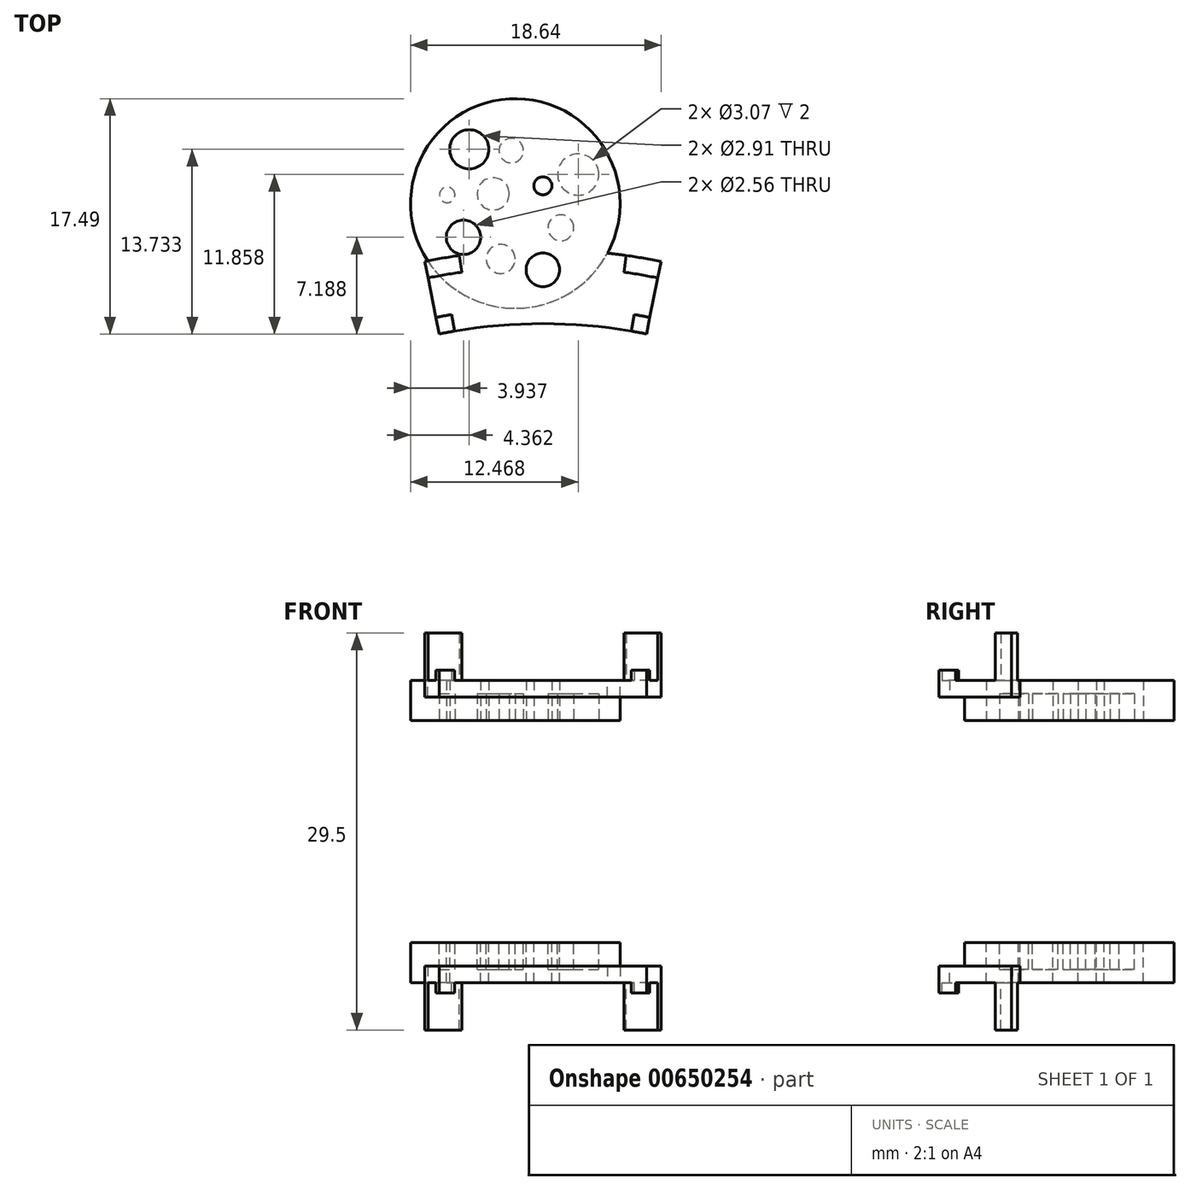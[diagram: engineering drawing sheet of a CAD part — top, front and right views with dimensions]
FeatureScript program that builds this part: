
annotation { "Feature Type Name" : "Feature", "Feature Type Description" : "" }
export const myFeature = defineFeature(function(context is Context, id is Id, definition is map)
    precondition{}
    {
        {
            var Q0;
            Q0=qCreatedBy(makeId("Top.planeOp"),FACE);
            var sketch = newSketch(context, id + "F0", { "sketchPlane" : qUnion([Q0])});
            skCircle(sketch, "E0", {"center": v(0, 0) * mm, "radius": 39 * mm});
            skCircle(sketch, "E1", {"center": v(0, 0) * mm, "radius": 44.5 * mm});
            skCircle(sketch, "E2", {"center": v(0, 43) * mm, "radius": 1.25 * mm});
            skCircle(sketch, "E3", {"center": v(0, 43) * mm, "radius": 6 * mm});
            skLineSegment(sketch, "E4", {"start": v(-7.7, 38.23) * mm, "end": v(-8.8, 43.62) * mm});
            skLineSegment(sketch, "E5", {"start": v(7.7, 38.23) * mm, "end": v(8.8, 43.62) * mm});
            skLineSegment(sketch, "E6", {"start": v(-7.5, 43.86) * mm, "end": v(-6.58, 38.44) * mm});
            skLineSegment(sketch, "E7", {"start": v(6.58, 38.44) * mm, "end": v(7.5, 43.86) * mm});
            skCircle(sketch, "E8", {"center": v(0, 0) * mm, "radius": 40.25 * mm});
            skCircle(sketch, "E9", {"center": v(0, 0) * mm, "radius": 43.25 * mm});
            skSolve(sketch);
        }
        {
            var Q0;
            {var subQ0=sQuery(id+"F0.wireOp",EDGE,"E7");var subQ1=sQuery(id+"F0.wireOp",EDGE,"E1");var subQ2=makeQuery(id+"F0.imprint","INTERSECT",VERTEX,{"derivedFrom":[subQ1,subQ0]});Q0=makeQuery(id+"F0.imprint","IMPRINT",FACE,{"disambiguationData":[TD([[makeQuery(id+"F0.imprint","IMPRINT",EDGE,{"disambiguationData":[TD([[subQ2,-1.0]])],"derivedFrom":subQ1}),1.0]])]});}
            var Q1;
            {var subQ0=sQuery(id+"F0.wireOp",EDGE,"E6");var subQ1=sQuery(id+"F0.wireOp",EDGE,"E1");var subQ2=makeQuery(id+"F0.imprint","INTERSECT",VERTEX,{"derivedFrom":[subQ1,subQ0]});Q1=makeQuery(id+"F0.imprint","IMPRINT",FACE,{"disambiguationData":[TD([[makeQuery(id+"F0.imprint","IMPRINT",EDGE,{"disambiguationData":[TD([[subQ2,1.0]])],"derivedFrom":subQ1}),1.0]])]});}
            var Q2;
            {var subQ0=sQuery(id+"F0.wireOp",EDGE,"E3");var subQ1=sQuery(id+"F0.wireOp",EDGE,"E1");var subQ2=makeQuery(id+"F0.imprint","INTERSECT",VERTEX,{"disambiguationData":[OD(0.0)],"derivedFrom":[subQ1,subQ0]});Q2=makeQuery(id+"F0.imprint","IMPRINT",FACE,{"disambiguationData":[TD([[makeQuery(id+"F0.imprint","IMPRINT",EDGE,{"disambiguationData":[TD([[subQ2,-1.0]])],"derivedFrom":subQ1}),1.0]])]});}
            var Q3;
            {var subQ0=sQuery(id+"F0.wireOp",EDGE,"E8");var subQ1=sQuery(id+"F0.wireOp",EDGE,"E3");var subQ2=makeQuery(id+"F0.imprint","INTERSECT",VERTEX,{"disambiguationData":[OD(1.0)],"derivedFrom":[subQ1,subQ0]});Q3=makeQuery(id+"F0.imprint","IMPRINT",FACE,{"disambiguationData":[TD([[makeQuery(id+"F0.imprint","IMPRINT",EDGE,{"disambiguationData":[TD([[subQ2,-1.0]])],"derivedFrom":subQ1}),-1.0]])]});}
            var Q4;
            {var subQ3=sQuery(id+"F0.wireOp",EDGE,"E9");var subQ5=sQuery(id+"F0.wireOp",EDGE,"E2");var subQ6=makeQuery(id+"F0.imprint","INTERSECT",VERTEX,{"disambiguationData":[OD(0.0)],"derivedFrom":[subQ5,subQ3]});Q4=makeQuery(id+"F0.imprint","IMPRINT",FACE,{"disambiguationData":[TD([[makeQuery(id+"F0.imprint","IMPRINT",EDGE,{"disambiguationData":[TD([[subQ6,1.0]])],"derivedFrom":subQ5}),-1.0]])]});}
            var Q5;
            {var subQ0=sQuery(id+"F0.wireOp",EDGE,"E9");var subQ1=sQuery(id+"F0.wireOp",EDGE,"E3");var subQ2=makeQuery(id+"F0.imprint","INTERSECT",VERTEX,{"disambiguationData":[OD(0.0)],"derivedFrom":[subQ1,subQ0]});Q5=makeQuery(id+"F0.imprint","IMPRINT",FACE,{"disambiguationData":[TD([[makeQuery(id+"F0.imprint","IMPRINT",EDGE,{"disambiguationData":[TD([[subQ2,-1.0]])],"derivedFrom":subQ1}),-1.0]])]});}
            var Q6;
            {var subQ0=sQuery(id+"F0.wireOp",EDGE,"E6");var subQ1=sQuery(id+"F0.wireOp",EDGE,"E0");var subQ2=makeQuery(id+"F0.imprint","INTERSECT",VERTEX,{"derivedFrom":[subQ1,subQ0]});Q6=makeQuery(id+"F0.imprint","IMPRINT",FACE,{"disambiguationData":[TD([[makeQuery(id+"F0.imprint","IMPRINT",EDGE,{"disambiguationData":[TD([[subQ2,1.0]])],"derivedFrom":subQ1}),-1.0]])]});}
            var Q7;
            {var subQ0=sQuery(id+"F0.wireOp",EDGE,"E3");var subQ1=sQuery(id+"F0.wireOp",EDGE,"E0");var subQ2=makeQuery(id+"F0.imprint","INTERSECT",VERTEX,{"disambiguationData":[OD(0.0)],"derivedFrom":[subQ1,subQ0]});Q7=makeQuery(id+"F0.imprint","IMPRINT",FACE,{"disambiguationData":[TD([[makeQuery(id+"F0.imprint","IMPRINT",EDGE,{"disambiguationData":[TD([[subQ2,-1.0]])],"derivedFrom":subQ1}),-1.0]])]});}
            var Q8;
            {var subQ0=sQuery(id+"F0.wireOp",EDGE,"E7");var subQ1=sQuery(id+"F0.wireOp",EDGE,"E0");var subQ2=makeQuery(id+"F0.imprint","INTERSECT",VERTEX,{"derivedFrom":[subQ1,subQ0]});Q8=makeQuery(id+"F0.imprint","IMPRINT",FACE,{"disambiguationData":[TD([[makeQuery(id+"F0.imprint","IMPRINT",EDGE,{"disambiguationData":[TD([[subQ2,-1.0]])],"derivedFrom":subQ1}),-1.0]])]});}
            var Q9;
            {var subQ0=sQuery(id+"F0.wireOp",EDGE,"E8");var subQ1=sQuery(id+"F0.wireOp",EDGE,"E5");var subQ2=makeQuery(id+"F0.imprint","INTERSECT",VERTEX,{"derivedFrom":[subQ1,subQ0]});Q9=makeQuery(id+"F0.imprint","IMPRINT",FACE,{"disambiguationData":[TD([[makeQuery(id+"F0.imprint","IMPRINT",EDGE,{"disambiguationData":[TD([[subQ2,-1.0]])],"derivedFrom":subQ1}),1.0]])]});}
            var Q10;
            {var subQ0=sQuery(id+"F0.wireOp",EDGE,"E8");var subQ1=sQuery(id+"F0.wireOp",EDGE,"E4");var subQ2=makeQuery(id+"F0.imprint","INTERSECT",VERTEX,{"derivedFrom":[subQ1,subQ0]});Q10=makeQuery(id+"F0.imprint","IMPRINT",FACE,{"disambiguationData":[TD([[makeQuery(id+"F0.imprint","IMPRINT",EDGE,{"disambiguationData":[TD([[subQ2,-1.0]])],"derivedFrom":subQ1}),-1.0]])]});}
            extrude(context, id + "F1", {"entities" : qUnion([Q0, Q1, Q2, Q3, Q4, Q5, Q6, Q7, Q8, Q9, Q10]), "depth" : 1.25 * mm, "offsetDistance" : 25 * mm});
        }
        {
            var Q0;
            Q0=qCreatedBy(makeId("Top.planeOp"),FACE);
            var sketch = newSketch(context, id + "F2", { "sketchPlane" : qUnion([Q0])});
            skCircle(sketch, "E10", {"center": v(0, 0) * mm, "radius": 39 * mm});
            skCircle(sketch, "E11", {"center": v(0, 0) * mm, "radius": 44.5 * mm});
            skCircle(sketch, "E12", {"center": v(0, 43) * mm, "radius": 0.85 * mm});
            skCircle(sketch, "E13", {"center": v(0, 43) * mm, "radius": 6 * mm});
            skLineSegment(sketch, "E14", {"start": v(-7.7, 38.23) * mm, "end": v(-8.8, 43.62) * mm});
            skLineSegment(sketch, "E15", {"start": v(7.7, 38.23) * mm, "end": v(8.8, 43.62) * mm});
            skLineSegment(sketch, "E16", {"start": v(-6.2, 44.06) * mm, "end": v(-5.44, 38.62) * mm});
            skLineSegment(sketch, "E17", {"start": v(5.44, 38.62) * mm, "end": v(6.2, 44.06) * mm});
            skCircle(sketch, "E18", {"center": v(0, 0) * mm, "radius": 40.25 * mm});
            skCircle(sketch, "E19", {"center": v(0, 0) * mm, "radius": 43.25 * mm});
            skSolve(sketch);
        }
        {
            var Q0;
            {var subQ0=sQuery(id+"F2.wireOp",EDGE,"E15");var subQ1=sQuery(id+"F2.wireOp",EDGE,"E11");var subQ2=makeQuery(id+"F2.imprint","INTERSECT",VERTEX,{"derivedFrom":[subQ1,subQ0]});Q0=makeQuery(id+"F2.imprint","IMPRINT",FACE,{"disambiguationData":[TD([[makeQuery(id+"F2.imprint","IMPRINT",EDGE,{"disambiguationData":[TD([[subQ2,-1.0]])],"derivedFrom":subQ1}),1.0]])]});}
            var Q1;
            {var subQ0=sQuery(id+"F2.wireOp",EDGE,"E14");var subQ1=sQuery(id+"F2.wireOp",EDGE,"E11");var subQ2=makeQuery(id+"F2.imprint","INTERSECT",VERTEX,{"derivedFrom":[subQ1,subQ0]});Q1=makeQuery(id+"F2.imprint","IMPRINT",FACE,{"disambiguationData":[TD([[makeQuery(id+"F2.imprint","IMPRINT",EDGE,{"disambiguationData":[TD([[subQ2,1.0]])],"derivedFrom":subQ1}),1.0]])]});}
            extrude(context, id + "F3", {"entities" : qUnion([Q0, Q1]), "operationType" : NewBodyOperationType.ADD, "depth" : 4.75 * mm, "offsetDistance" : 25 * mm});
        }
        {
            var Q0;
            Q0=qCreatedBy(makeId("Top.planeOp"),FACE);
            var sketch = newSketch(context, id + "F4", { "sketchPlane" : qUnion([Q0])});
            skCircle(sketch, "E20", {"center": v(0, 0) * mm, "radius": 39 * mm});
            skCircle(sketch, "E21", {"center": v(0, 0) * mm, "radius": 44.5 * mm});
            skCircle(sketch, "E22", {"center": v(0, 43) * mm, "radius": 0.85 * mm});
            skCircle(sketch, "E23", {"center": v(0, 43) * mm, "radius": 6 * mm});
            skLineSegment(sketch, "E24", {"start": v(-7.7, 38.23) * mm, "end": v(-8.8, 43.62) * mm});
            skLineSegment(sketch, "E25", {"start": v(7.7, 38.23) * mm, "end": v(8.8, 43.62) * mm});
            skLineSegment(sketch, "E26", {"start": v(-7.5, 43.86) * mm, "end": v(-6.58, 38.44) * mm});
            skLineSegment(sketch, "E27", {"start": v(6.58, 38.44) * mm, "end": v(7.5, 43.86) * mm});
            skCircle(sketch, "E28", {"center": v(0, 0) * mm, "radius": 40.25 * mm});
            skCircle(sketch, "E29", {"center": v(0, 0) * mm, "radius": 43.25 * mm});
            skSolve(sketch);
        }
        {
            var Q0;
            {var subQ0=sQuery(id+"F4.wireOp",EDGE,"E24");var subQ1=sQuery(id+"F4.wireOp",EDGE,"E20");var subQ2=makeQuery(id+"F4.imprint","INTERSECT",VERTEX,{"derivedFrom":[subQ1,subQ0]});Q0=makeQuery(id+"F4.imprint","IMPRINT",FACE,{"disambiguationData":[TD([[makeQuery(id+"F4.imprint","IMPRINT",EDGE,{"disambiguationData":[TD([[subQ2,1.0]])],"derivedFrom":subQ1}),-1.0]])]});}
            var Q1;
            {var subQ0=sQuery(id+"F4.wireOp",EDGE,"E25");var subQ1=sQuery(id+"F4.wireOp",EDGE,"E20");var subQ2=makeQuery(id+"F4.imprint","INTERSECT",VERTEX,{"derivedFrom":[subQ1,subQ0]});Q1=makeQuery(id+"F4.imprint","IMPRINT",FACE,{"disambiguationData":[TD([[makeQuery(id+"F4.imprint","IMPRINT",EDGE,{"disambiguationData":[TD([[subQ2,-1.0]])],"derivedFrom":subQ1}),-1.0]])]});}
            extrude(context, id + "F5", {"entities" : qUnion([Q0, Q1]), "operationType" : NewBodyOperationType.ADD, "depth" : 2 * mm, "offsetDistance" : 25 * mm});
        }
        {
            var Q0;
            Q0=makeQuery(id+"F1.opExtrude","CAP_FACE",FACE,{"disambiguationData":[OSD([sQuery(id+"F0.wireOp",EDGE,"E0"),sQuery(id+"F0.wireOp",EDGE,"E1"),sQuery(id+"F0.wireOp",EDGE,"E2"),sQuery(id+"F0.wireOp",EDGE,"E4"),sQuery(id+"F0.wireOp",EDGE,"E5"),sQuery(id+"F0.wireOp",EDGE,"E6"),sQuery(id+"F0.wireOp",EDGE,"E7"),sQuery(id+"F0.wireOp",EDGE,"E8"),sQuery(id+"F0.wireOp",EDGE,"E9")])],"isStart":false});
            var sketch = newSketch(context, id + "F6", { "sketchPlane" : qUnion([Q0])});
            skCircle(sketch, "E30", {"center": v(-2.05, 47.93) * mm, "radius": 7.8 * mm});
            skSolve(sketch);
        }
        {
            var Q0;
            {var subQ1=sQuery(id+"F0.wireOp",EDGE,"E1");var subQ5=sQuery(id+"F2.wireOp",EDGE,"E16");var subQ6=makeQuery(id+"F1.opExtrude","CAP_FACE",FACE,{"disambiguationData":[OSD([sQuery(id+"F0.wireOp",EDGE,"E0"),subQ1,sQuery(id+"F0.wireOp",EDGE,"E2"),sQuery(id+"F0.wireOp",EDGE,"E4"),sQuery(id+"F0.wireOp",EDGE,"E5"),sQuery(id+"F0.wireOp",EDGE,"E6"),sQuery(id+"F0.wireOp",EDGE,"E7"),sQuery(id+"F0.wireOp",EDGE,"E8"),sQuery(id+"F0.wireOp",EDGE,"E9")])],"isStart":false});var subQ9=makeQuery(id+"F3.boolean.opBoolean","INTERSECT",EDGE,{"derivedFrom":[subQ6,makeQuery(id+"F3.opExtrude","SWEPT_FACE",FACE,{"disambiguationData":[OSD([subQ5])]})]});Q0=makeQuery(id+"F6.imprint","IMPRINT",FACE,{"disambiguationData":[TD([[makeQuery(id+"F6.imprint","IMPRINT",EDGE,{"derivedFrom":subQ9}),1.0]])]});}
            var Q1;
            {var subQ1=sQuery(id+"F0.wireOp",EDGE,"E2");Q1=makeQuery(id+"F6.imprint","IMPRINT",FACE,{"disambiguationData":[TD([[makeQuery(id+"F6.imprint","IMPRINT",EDGE,{"derivedFrom":makeQuery(id+"F1.opExtrude","CAP_EDGE",EDGE,{"disambiguationData":[OSD([subQ1])],"isStart":false})}),-1.0]])]});}
            var Q2;
            Q2=sQuery(id+"F6.wireOp",EDGE,"E30");
            extrude(context, id + "F7", {"entities" : qUnion([Q0, Q1]), "operationType" : NewBodyOperationType.ADD, "surfaceEntities" : qUnion([Q2]), "oppositeDirection" : true, "depth" : 3 * mm, "offsetDistance" : 25 * mm});
        }
        {
            var Q0;
            Q0=makeQuery(id+"F7.opExtrude","CAP_FACE",FACE,{"disambiguationData":[OSD([sQuery(id+"F0.wireOp",EDGE,"E2"),sQuery(id+"F6.wireOp",EDGE,"E30")])],"isStart":false});
            var sketch = newSketch(context, id + "F8", { "sketchPlane" : qUnion([Q0])});
            skCircle(sketch, "E31", {"center": v(2.63, -50.09) * mm, "radius": 1.53 * mm});
            skCircle(sketch, "E32", {"center": v(-2.35, -51.86) * mm, "radius": 0.9 * mm});
            skCircle(sketch, "E33", {"center": v(-7.12, -48.57) * mm, "radius": 0.58 * mm});
            skCircle(sketch, "E34", {"center": v(-3.14, -43.8) * mm, "radius": 1.08 * mm});
            skCircle(sketch, "E35", {"center": v(-3.7, -48.65) * mm, "radius": 1.2 * mm});
            skCircle(sketch, "E36", {"center": v(1.34, -46.12) * mm, "radius": 0.96 * mm});
            skSolve(sketch);
        }
        {
            var Q0;
            Q0 = qSketchRegion(id + "F8", true);
            extrude(context, id + "F9", {"entities" : qUnion([Q0]), "operationType" : NewBodyOperationType.REMOVE, "oppositeDirection" : true, "depth" : 2 * mm, "offsetDistance" : 25 * mm});
        }
        {
            var Q0;
            Q0=makeQuery(id+"F7.opExtrude","CAP_FACE",FACE,{"disambiguationData":[OSD([sQuery(id+"F0.wireOp",EDGE,"E2"),sQuery(id+"F6.wireOp",EDGE,"E30")])],"isStart":false});
            var sketch = newSketch(context, id + "F10", { "sketchPlane" : qUnion([Q0])});
            skCircle(sketch, "E37", {"center": v(-5.9, -45.42) * mm, "radius": 1.28 * mm});
            skCircle(sketch, "E38", {"center": v(0, -49.25) * mm, "radius": 0.67 * mm});
            skCircle(sketch, "E39", {"center": v(-5.48, -51.96) * mm, "radius": 1.46 * mm});
            skSolve(sketch);
        }
        {
            var Q0;
            Q0 = qSketchRegion(id + "F10", true);
            extrude(context, id + "F11", {"entities" : qUnion([Q0]), "operationType" : NewBodyOperationType.REMOVE, "oppositeDirection" : true, "depth" : 25 * mm, "offsetDistance" : 25 * mm});
        }
        {
            var Q0;
            Q0=makeQuery(id+"F1.opExtrude","SWEPT_BODY",BODY,{"disambiguationData":[OSD([sQuery(id+"F0.wireOp",EDGE,"E0"),sQuery(id+"F0.wireOp",EDGE,"E1"),sQuery(id+"F0.wireOp",EDGE,"E2"),sQuery(id+"F0.wireOp",EDGE,"E4"),sQuery(id+"F0.wireOp",EDGE,"E5"),sQuery(id+"F0.wireOp",EDGE,"E6"),sQuery(id+"F0.wireOp",EDGE,"E7"),sQuery(id+"F0.wireOp",EDGE,"E8"),sQuery(id+"F0.wireOp",EDGE,"E9")])]});
            transform(context, id + "F12", {"entities" : qUnion([Q0]), "transformType" : TransformType.TRANSLATION_3D, "dx" : 0 * mm, "dy" : 0 * mm, "dz" : 10 * mm, "makeCopy" : false});
        }
        {
            var Q0;
            Q0=makeQuery(id+"F1.opExtrude","SWEPT_BODY",BODY,{"disambiguationData":[OSD([sQuery(id+"F0.wireOp",EDGE,"E0"),sQuery(id+"F0.wireOp",EDGE,"E1"),sQuery(id+"F0.wireOp",EDGE,"E2"),sQuery(id+"F0.wireOp",EDGE,"E4"),sQuery(id+"F0.wireOp",EDGE,"E5"),sQuery(id+"F0.wireOp",EDGE,"E6"),sQuery(id+"F0.wireOp",EDGE,"E7"),sQuery(id+"F0.wireOp",EDGE,"E8"),sQuery(id+"F0.wireOp",EDGE,"E9")])]});
            var Q1;
            Q1=qCreatedBy(makeId("Top.planeOp"),FACE);
            mirror(context, id + "F13", {"entities" : qUnion([Q0]), "mirrorPlane" : qUnion([Q1])});
        }
    });
